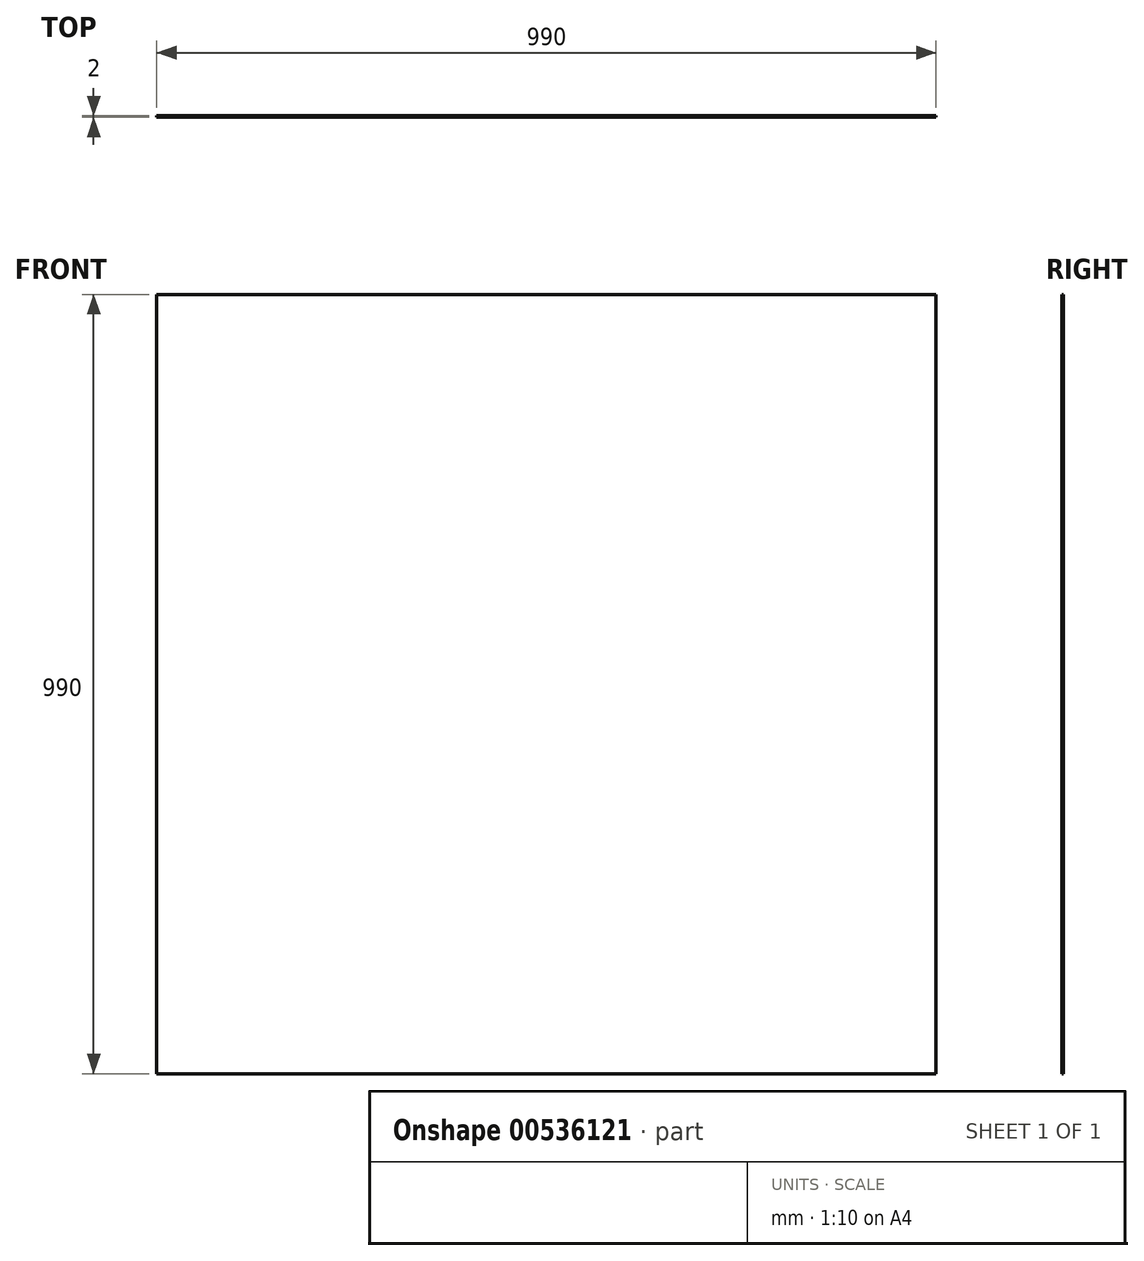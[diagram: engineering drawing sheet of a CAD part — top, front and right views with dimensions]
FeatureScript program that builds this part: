
annotation { "Feature Type Name" : "Feature", "Feature Type Description" : "" }
export const myFeature = defineFeature(function(context is Context, id is Id, definition is map)
    precondition{}
    {
        {
            var Q0;
            Q0=qCreatedBy(makeId("Front.planeOp"),FACE);
            var sketch = newSketch(context, id + "F0", { "sketchPlane" : qUnion([Q0])});
            skLineSegment(sketch, "E0.bottom", {"start": v(495, 495) * mm, "end": v(-495, 495) * mm});
            skLineSegment(sketch, "E0.top", {"start": v(495, -495) * mm, "end": v(-495, -495) * mm});
            skLineSegment(sketch, "E0.left", {"start": v(495, 495) * mm, "end": v(495, -495) * mm});
            skLineSegment(sketch, "E0.right", {"start": v(-495, 495) * mm, "end": v(-495, -495) * mm});
            skPoint(sketch, "E0.middle", {"position": v(0, 0) * mm});
            skSolve(sketch);
        }
        {
            var Q0;
            Q0=makeQuery(id+"F0.imprint","IMPRINT",FACE,{"disambiguationData":[TD([[makeQuery(id+"F0.imprint","IMPRINT",EDGE,{"derivedFrom":sQuery(id+"F0.wireOp",EDGE,"E0.bottom")}),1.0]])]});
            extrude(context, id + "F1", {"entities" : qUnion([Q0]), "endBound" : BoundingType.SYMMETRIC, "depth" : 2 * mm, "offsetDistance" : 25 * mm});
        }
    });
